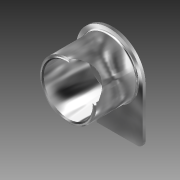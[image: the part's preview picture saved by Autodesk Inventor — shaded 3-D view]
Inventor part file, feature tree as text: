
AUTODESK INVENTOR PART (.ipt)
format: ipt  version: 2014 (Build 180170000, 170)  size: 144,384 bytes
history: native  units: mm (DEFAULTED — no unit token found)
features: reference x6, plane x3, extrude x3, sketch x3, chamfer x2, fillet x1
ambient origin geometry x8: Origin, YZ Plane, XZ Plane, XY Plane, X Axis, Y Axis, Z Axis, Center Point
bodies: Solid1 (feature_tree)
feature tree (18):
  plane  "Work Plane1"
  plane  "Work Plane2"
  plane  "Work Plane3"
  extrude  "Extrusion2"  Depth=0.127mm
  chamfer  "Chamfer2"  Distance=9.525mm
  extrude  "Extrusion3"  Depth=9.525mm TaperAngle=0.0deg
  extrude  "Extrusion4"  Depth=0.381mm
  chamfer  "Chamfer3"  Distance=0.381mm
  fillet  "Fillet1"  [1 undecoded]
  sketch  "Sketch1"  dims[d6=25.4mm d7=0.0mm d8=0.127mm d9=0.127mm]
  reference  "Reference2"
  reference  "Reference3"
  reference  "Reference4"
  reference  "Reference5"
  reference  "Reference6"
  reference  "Reference7"
  sketch  "Sketch3"  dims[d10=12.7mm d11=9.525mm d12=0.0mm]
  sketch  "Sketch4"  dims[d13=11.1125mm d14=9.525mm d15=0.0mm d16=0.254mm d17=0.254mm d18=0.381mm d19=45.0deg d20=45.0deg]
note: 1 required parameter value undecoded (feature->parameter linkage not recoverable at this tier; creation-order binding heuristic only, values carry confidence <= 0.55)
